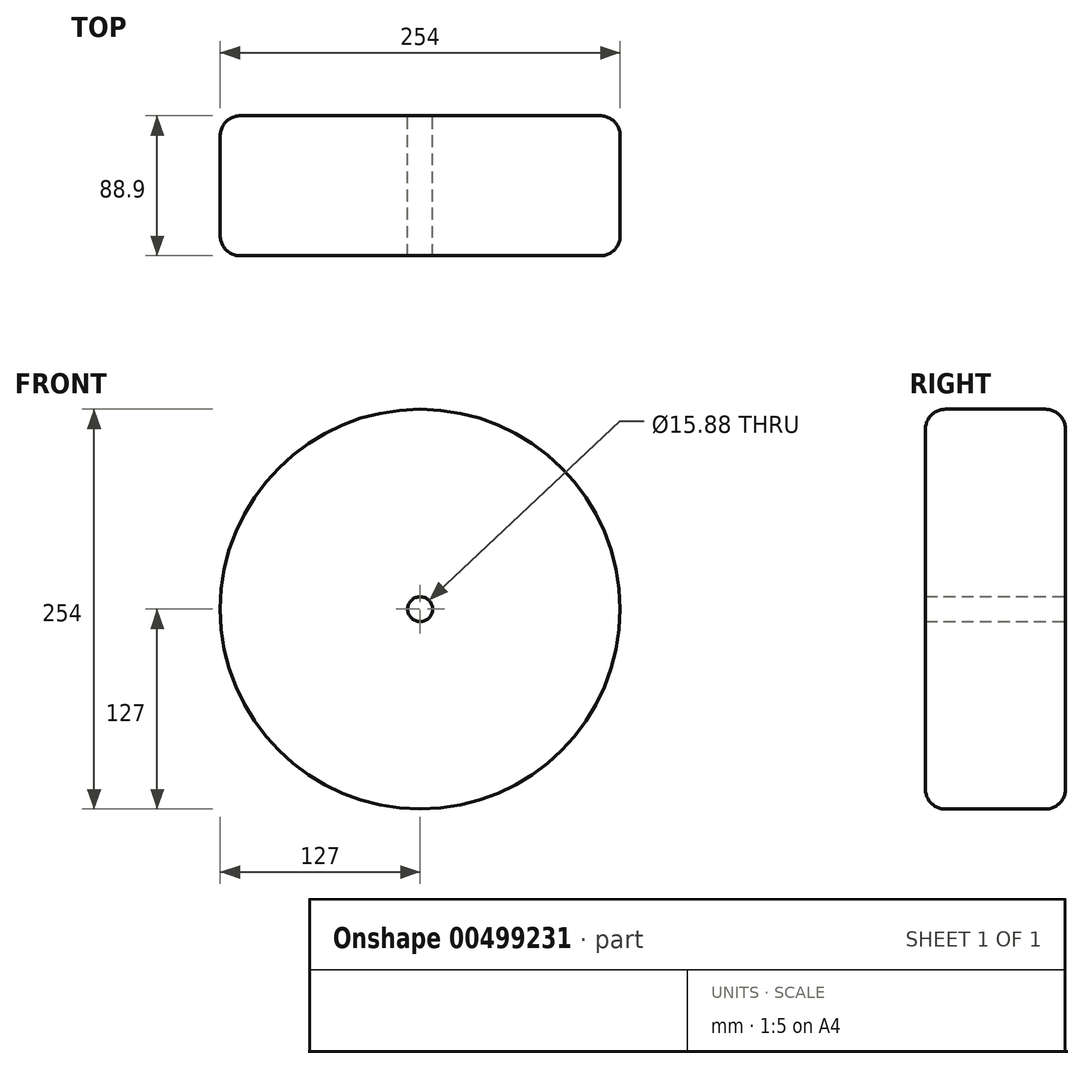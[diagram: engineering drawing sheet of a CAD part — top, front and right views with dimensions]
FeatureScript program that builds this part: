
annotation { "Feature Type Name" : "Feature", "Feature Type Description" : "" }
export const myFeature = defineFeature(function(context is Context, id is Id, definition is map)
    precondition{}
    {
        {
            var Q0;
            Q0=qCreatedBy(makeId("Front.planeOp"),FACE);
            var sketch = newSketch(context, id + "F0", { "sketchPlane" : qUnion([Q0])});
            skCircle(sketch, "E0", {"center": v(0, 0) * mm, "radius": 127 * mm});
            skCircle(sketch, "E1", {"center": v(0, 0) * mm, "radius": 7.94 * mm});
            skSolve(sketch);
        }
        {
            var Q0;
            Q0 = qSketchRegion(id + "F0", true);
            extrude(context, id + "F1", {"entities" : qUnion([Q0]), "depth" : 88.9 * mm, "offsetDistance" : 25.4 * mm});
        }
        {
            var Q0;
            Q0=makeQuery(id+"F1.opExtrude","CAP_EDGE",EDGE,{"disambiguationData":[OSD([sQuery(id+"F0.wireOp",EDGE,"E0")])],"isStart":false});
            var Q1;
            Q1=makeQuery(id+"F1.opExtrude","CAP_EDGE",EDGE,{"disambiguationData":[OSD([sQuery(id+"F0.wireOp",EDGE,"E0")])],"isStart":true});
            fillet(context, id + "F2", {"entities" : qUnion([Q0, Q1]), "radius" : 12.7 * mm, "tangentPropagation" : true, "allowEdgeOverflow" : false});
        }
    });
